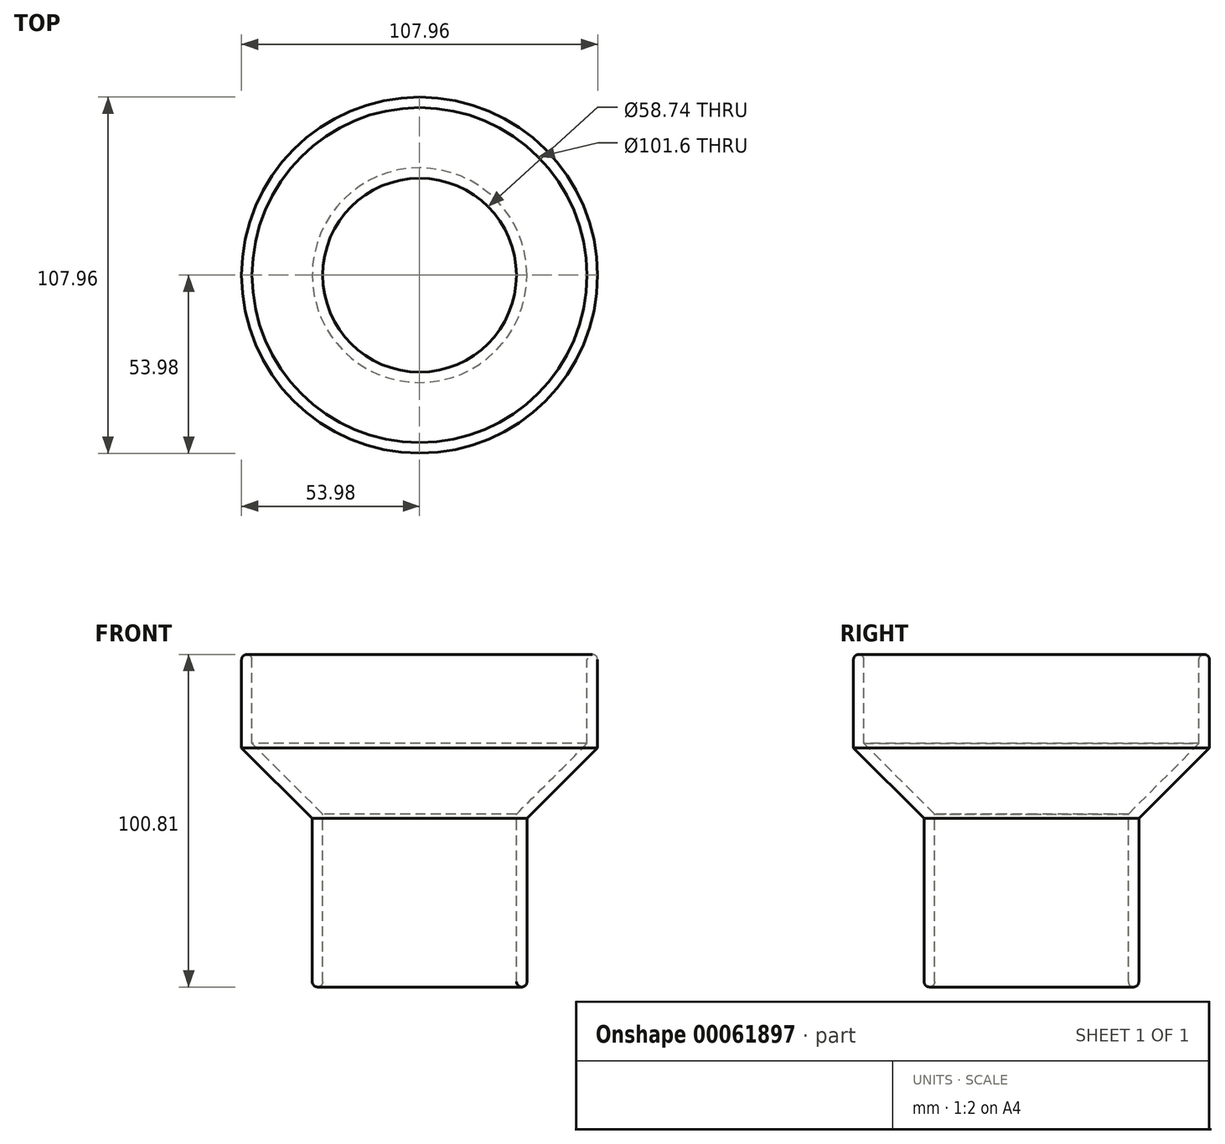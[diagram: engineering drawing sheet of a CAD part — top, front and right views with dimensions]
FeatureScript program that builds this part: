
annotation { "Feature Type Name" : "Feature", "Feature Type Description" : "" }
export const myFeature = defineFeature(function(context is Context, id is Id, definition is map)
    precondition{}
    {
        {
            var Q0;
            Q0=qCreatedBy(makeId("Front.planeOp"),FACE);
            var sketch = newSketch(context, id + "F0", { "sketchPlane" : qUnion([Q0])});
            skLineSegment(sketch, "E0", {"start": v(29.37, 1.59) * mm, "end": v(29.37, 52.39) * mm});
            skLineSegment(sketch, "E1", {"start": v(29.37, 52.39) * mm, "end": v(50.8, 73.82) * mm});
            skLineSegment(sketch, "E2", {"start": v(50.8, 73.82) * mm, "end": v(50.8, 99.22) * mm});
            skLineSegment(sketch, "E3.0", {"start": v(53.98, 72.5) * mm, "end": v(53.98, 99.22) * mm});
            skLineSegment(sketch, "E3.1", {"start": v(32.54, 51.07) * mm, "end": v(53.98, 72.5) * mm});
            skLineSegment(sketch, "E3.2", {"start": v(32.54, 1.59) * mm, "end": v(32.54, 51.07) * mm});
            skArc(sketch, "E4", {"start": v(53.98, 99.22) * mm, "mid": v(52.39, 100.8) * mm, "end": v(50.8, 99.22) * mm});
            skArc(sketch, "E5", {"start": v(29.37, 1.59) * mm, "mid": v(30.96, 0) * mm, "end": v(32.54, 1.59) * mm});
            skLineSegment(sketch, "E6", {"start": v(0, 56.78) * mm, "end": v(0, -13.5) * mm, "construction": true});
            skSolve(sketch);
        }
        {
            var Q0;
            Q0=makeQuery(id+"F0.imprint","IMPRINT",FACE,{"disambiguationData":[TD([[makeQuery(id+"F0.imprint","IMPRINT",EDGE,{"derivedFrom":sQuery(id+"F0.wireOp",EDGE,"E0")}),-1.0]])]});
            var Q1;
            Q1=sQuery(id+"F0.wireOp",EDGE,"E6");
            revolve(context, id + "F1", {"entities" : qUnion([Q0]), "axis" : qUnion([Q1]), "revolveType" : RevolveType.FULL});
        }
    });
